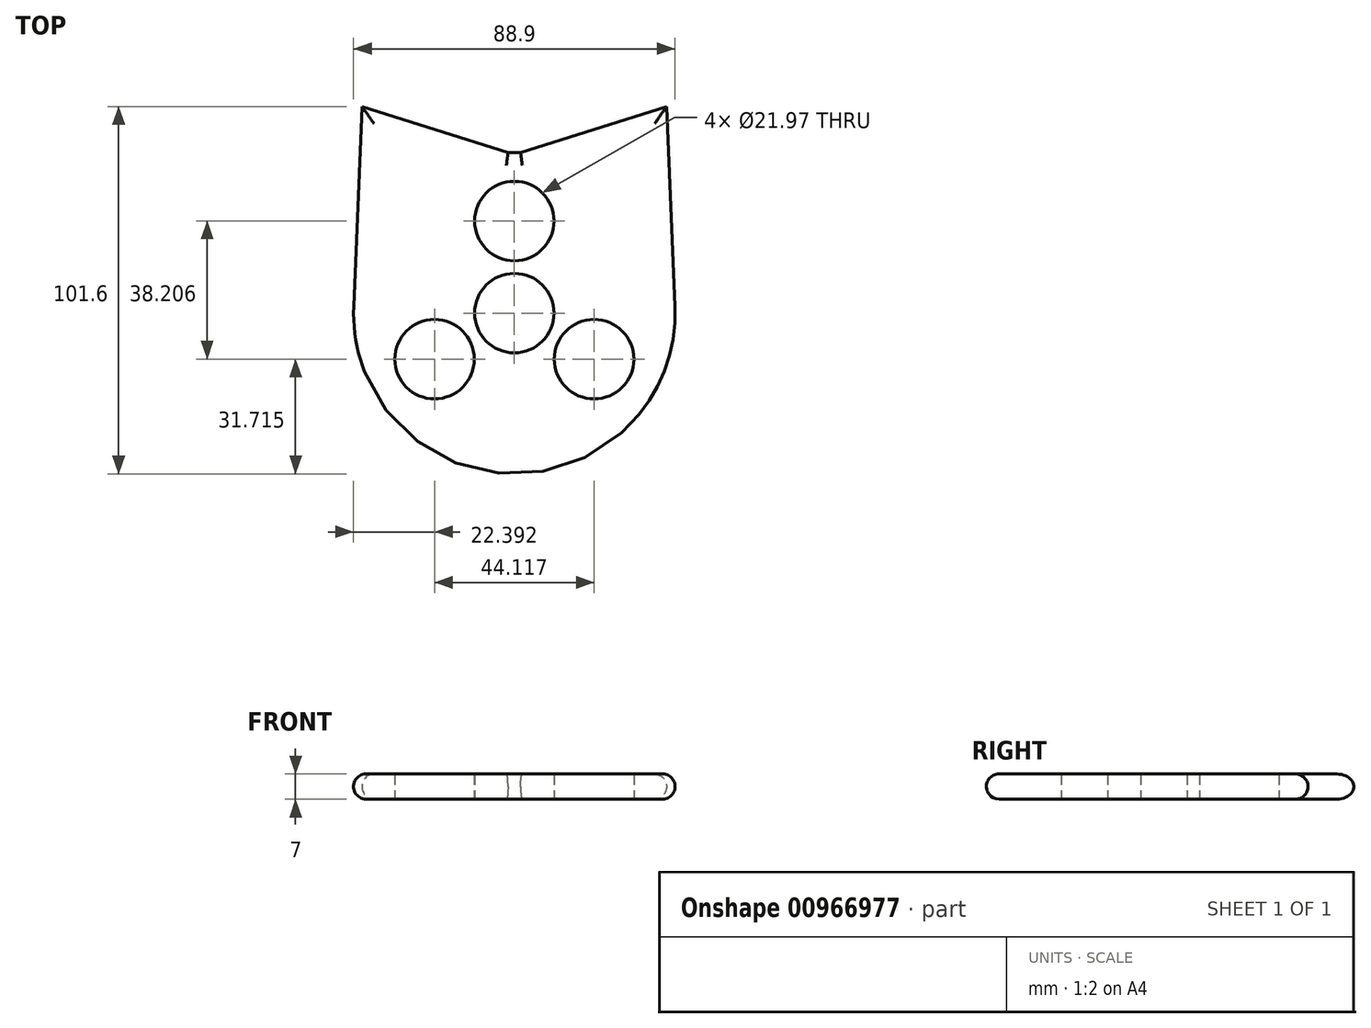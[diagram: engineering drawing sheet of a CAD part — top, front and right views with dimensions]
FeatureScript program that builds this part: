
annotation { "Feature Type Name" : "Feature", "Feature Type Description" : "" }
export const myFeature = defineFeature(function(context is Context, id is Id, definition is map)
    precondition{}
    {
        {
            var Q0;
            Q0=qCreatedBy(makeId("Top.planeOp"),FACE);
            var sketch = newSketch(context, id + "F0", { "sketchPlane" : qUnion([Q0])});
            skCircle(sketch, "E0", {"center": v(0, 0) * mm, "radius": 10.99 * mm});
            skCircle(sketch, "E1", {"center": v(0, 0) * mm, "radius": 25.47 * mm, "construction": true});
            skCircle(sketch, "E2", {"center": v(0, 25.47) * mm, "radius": 10.99 * mm});
            skCircle(sketch, "E3", {"center": v(-22.06, -12.74) * mm, "radius": 10.99 * mm});
            skCircle(sketch, "E4", {"center": v(22.06, -12.74) * mm, "radius": 10.99 * mm});
            skLineSegment(sketch, "E5", {"start": v(-22.06, -12.74) * mm, "end": v(22.06, -12.74) * mm, "construction": true});
            skLineSegment(sketch, "E6", {"start": v(0, 25.47) * mm, "end": v(-22.06, -12.74) * mm, "construction": true});
            skLineSegment(sketch, "E7", {"start": v(22.06, -12.74) * mm, "end": v(0, 25.47) * mm, "construction": true});
            skLineSegment(sketch, "E8.bottom", {"start": v(-57.15, 57.15) * mm, "end": v(57.15, 57.15) * mm, "construction": true});
            skLineSegment(sketch, "E8.top", {"start": v(-57.15, -57.15) * mm, "end": v(57.15, -57.15) * mm, "construction": true});
            skLineSegment(sketch, "E8.left", {"start": v(-57.15, 57.15) * mm, "end": v(-57.15, -57.15) * mm, "construction": true});
            skLineSegment(sketch, "E8.right", {"start": v(57.15, 57.15) * mm, "end": v(57.15, -57.15) * mm, "construction": true});
            skPoint(sketch, "E9", {"position": v(-57.15, 0) * mm});
            skPoint(sketch, "E10", {"position": v(0, 57.15) * mm});
            skSolve(sketch);
        }
        {
            var Q0;
            Q0=qCreatedBy(makeId("Top.planeOp"),FACE);
            var sketch = newSketch(context, id + "F1", { "sketchPlane" : qUnion([Q0])});
            skCircle(sketch, "E11", {"center": v(0, 0) * mm, "radius": 10.99 * mm});
            skCircle(sketch, "E12", {"center": v(-22.06, -12.74) * mm, "radius": 10.99 * mm});
            skCircle(sketch, "E13", {"center": v(0, 25.47) * mm, "radius": 10.99 * mm});
            skCircle(sketch, "E14", {"center": v(22.06, -12.74) * mm, "radius": 10.99 * mm});
            skLineSegment(sketch, "E15.bottom", {"start": v(-57.15, 57.15) * mm, "end": v(57.15, 57.15) * mm, "construction": true});
            skLineSegment(sketch, "E15.top", {"start": v(-57.15, -57.15) * mm, "end": v(57.15, -57.15) * mm, "construction": true});
            skLineSegment(sketch, "E15.left", {"start": v(-57.15, 57.15) * mm, "end": v(-57.15, -57.15) * mm, "construction": true});
            skLineSegment(sketch, "E15.right", {"start": v(57.15, 57.15) * mm, "end": v(57.15, -57.15) * mm, "construction": true});
            skPoint(sketch, "E16", {"position": v(-57.15, 0) * mm});
            skPoint(sketch, "E17", {"position": v(0, 57.15) * mm});
            skCircle(sketch, "E18", {"center": v(0, 0) * mm, "radius": 44.45 * mm});
            skLineSegment(sketch, "E19", {"start": v(-1.73, 44.42) * mm, "end": v(-42.13, 57.15) * mm});
            skLineSegment(sketch, "E20", {"start": v(-42.13, 57.15) * mm, "end": v(-44.41, 1.83) * mm});
            skLineSegment(sketch, "E21", {"start": v(1.73, 44.42) * mm, "end": v(42.13, 57.15) * mm});
            skLineSegment(sketch, "E22", {"start": v(42.13, 57.15) * mm, "end": v(44.41, 1.83) * mm});
            skLineSegment(sketch, "E23", {"start": v(-1.73, 44.42) * mm, "end": v(1.73, 44.42) * mm, "construction": true});
            skLineSegment(sketch, "E24", {"start": v(0, 44.42) * mm, "end": v(0, 0) * mm, "construction": true});
            skSolve(sketch);
        }
        {
            var Q0;
            Q0 = qSketchRegion(id + "F1", true);
            extrude(context, id + "F2", {"entities" : qUnion([Q0]), "depth" : 7 * mm, "offsetDistance" : 25.4 * mm});
        }
        {
            var Q0;
            Q0=makeQuery(id+"F2.opExtrude","CAP_EDGE",EDGE,{"disambiguationData":[OSD([sQuery(id+"F1.wireOp",EDGE,"E22")])],"isStart":false});
            var Q1;
            Q1=makeQuery(id+"F2.opExtrude","CAP_EDGE",EDGE,{"disambiguationData":[OSD([sQuery(id+"F1.wireOp",EDGE,"E22")])],"isStart":true});
            var Q2;
            Q2=makeQuery(id+"F2.opExtrude","CAP_EDGE",EDGE,{"disambiguationData":[OSD([sQuery(id+"F1.wireOp",EDGE,"E19")])],"isStart":false});
            var Q3;
            Q3=makeQuery(id+"F2.opExtrude","CAP_EDGE",EDGE,{"disambiguationData":[OSD([sQuery(id+"F1.wireOp",EDGE,"E21")])],"isStart":false});
            var Q4;
            Q4=makeQuery(id+"F2.opExtrude","CAP_EDGE",EDGE,{"disambiguationData":[OSD([sQuery(id+"F1.wireOp",EDGE,"E21")])],"isStart":true});
            var Q5;
            Q5=makeQuery(id+"F2.opExtrude","CAP_EDGE",EDGE,{"disambiguationData":[OSD([sQuery(id+"F1.wireOp",EDGE,"E19")])],"isStart":true});
            var Q6;
            {var subQ0=sQuery(id+"F1.wireOp",EDGE,"E18");Q6=makeQuery(id+"F2.opExtrude","CAP_EDGE",EDGE,{"disambiguationData":[OSD([subQ0]),TDD([makeQuery(id+"F1.imprint","IMPRINT",EDGE,{"disambiguationData":[TD([[makeQuery(id+"F1.imprint","INTERSECT",VERTEX,{"derivedFrom":[subQ0,sQuery(id+"F1.wireOp",EDGE,"E19")]}),1.0]])],"derivedFrom":subQ0})])],"isStart":true});}
            var Q7;
            {var subQ0=sQuery(id+"F1.wireOp",EDGE,"E18");Q7=makeQuery(id+"F2.opExtrude","CAP_EDGE",EDGE,{"disambiguationData":[OSD([subQ0]),TDD([makeQuery(id+"F1.imprint","IMPRINT",EDGE,{"disambiguationData":[TD([[makeQuery(id+"F1.imprint","INTERSECT",VERTEX,{"derivedFrom":[subQ0,sQuery(id+"F1.wireOp",EDGE,"E19")]}),1.0]])],"derivedFrom":subQ0})])],"isStart":false});}
            fillet(context, id + "F3", {"entities" : qUnion([Q0, Q1, Q2, Q3, Q4, Q5, Q6, Q7]), "radius" : 3.5 * mm, "tangentPropagation" : true, "allowEdgeOverflow" : false});
        }
    });
